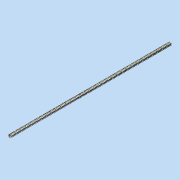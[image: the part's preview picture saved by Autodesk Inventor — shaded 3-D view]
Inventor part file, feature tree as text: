
AUTODESK INVENTOR PART (.ipt)
format: ipt  version: 2015 (Build 190159000, 159)  size: 1,125,376 bytes
history: native  units: in
note: dims shown in document units (in); Inventor stores cm internally (conversion verified against a paired STEP export)
features: sketch x5, helix x4, extrude x1, other x1
ambient origin geometry x8: Origin, YZ Plane, XZ Plane, XY Plane, X Axis, Y Axis, Z Axis, Center Point
bodies: Solid1 (feature_tree)
feature tree (11):
  extrude  "Extrusion1"  Depth=15.9449in TaperAngle=0.0deg
  helix  "Coil2"  [1 undecoded]
  helix  "Coil6"  [1 undecoded]
  helix  "Coil7"  [1 undecoded]
  helix  "Coil8"  [1 undecoded]
  other  "Move Face1"
  sketch  "Sketch1"  dims[d0=0.315in d1=15.9449in d2=0.0in d3=0.1993in d4=0.0996in d5=0.0in d6=0.7181in]
  sketch  "Sketch2"  dims[d9=0.0411in]
  sketch  "Sketch9"  dims[d10=0.0725in]
  sketch  "Sketch10"  dims[d20=0.5in d21=1.0in d22=19.685in d23=0.0in d24=90.0deg d25=90.0deg d26=0.0in d27=0.0in]
  sketch  "Sketch11"  dims[d91=15.0deg d92=30.0deg d93=0.0411in d94=0.125in d95=0.0725in d96=0.5in d97=1.0in d98=19.685in d99=0.0in d100=90.0deg d101=90.0deg d102=0.0in d103=0.0in d105=30.0deg d107=0.0725in d108=0.0411in d109=0.5in d110=1.0in d111=19.685in d112=0.0in d113=90.0deg d114=90.0deg d115=0.0in d116=0.0in d118=30.0deg d119=0.0725in d120=0.0411in d122=0.5in d123=1.0in d124=19.685in d125=0.0in d126=90.0deg d127=90.0deg d128=0.0in d129=0.0in]
note: 4 required parameter values undecoded (feature->parameter linkage not recoverable at this tier; creation-order binding heuristic only, values carry confidence <= 0.55)
